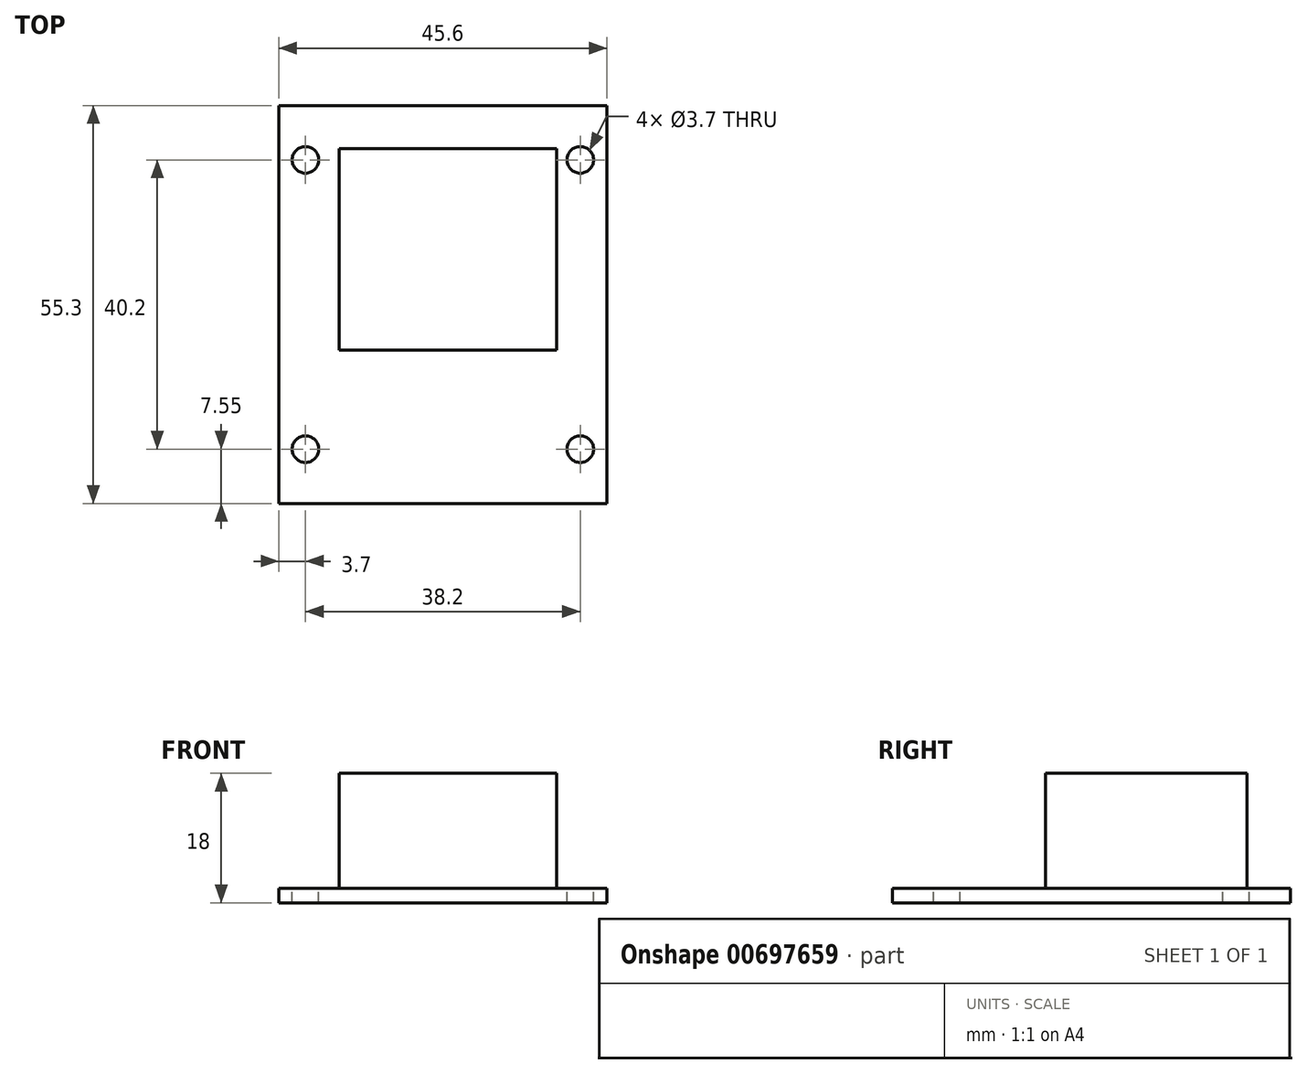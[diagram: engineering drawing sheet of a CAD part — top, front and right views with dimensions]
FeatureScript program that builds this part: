
annotation { "Feature Type Name" : "Feature", "Feature Type Description" : "" }
export const myFeature = defineFeature(function(context is Context, id is Id, definition is map)
    precondition{}
    {
        {
            var Q0;
            Q0=qCreatedBy(makeId("Top.planeOp"),FACE);
            var sketch = newSketch(context, id + "F0", { "sketchPlane" : qUnion([Q0])});
            skLineSegment(sketch, "E0.bottom", {"start": v(22.8, -27.65) * mm, "end": v(-22.8, -27.65) * mm});
            skLineSegment(sketch, "E0.top", {"start": v(22.8, 27.65) * mm, "end": v(-22.8, 27.65) * mm});
            skLineSegment(sketch, "E0.left", {"start": v(22.8, -27.65) * mm, "end": v(22.8, 27.65) * mm});
            skLineSegment(sketch, "E0.right", {"start": v(-22.8, -27.65) * mm, "end": v(-22.8, 27.65) * mm});
            skPoint(sketch, "E0.middle", {"position": v(0, 0) * mm});
            skSolve(sketch);
        }
        {
            var Q0;
            Q0 = qSketchRegion(id + "F0", true);
            extrude(context, id + "F1", {"entities" : qUnion([Q0]), "depth" : 2 * mm, "offsetDistance" : 25 * mm});
        }
        {
            var Q0;
            Q0=makeQuery(id+"F1.opExtrude","CAP_FACE",FACE,{"disambiguationData":[OSD([sQuery(id+"F0.wireOp",EDGE,"E0.bottom"),sQuery(id+"F0.wireOp",EDGE,"E0.top"),sQuery(id+"F0.wireOp",EDGE,"E0.left"),sQuery(id+"F0.wireOp",EDGE,"E0.right")])],"isStart":false});
            var sketch = newSketch(context, id + "F2", { "sketchPlane" : qUnion([Q0])});
            skCircle(sketch, "E1", {"center": v(-19.1, 20.1) * mm, "radius": 1.85 * mm});
            skCircle(sketch, "E2.MirrorC", {"center": v(19.1, 20.1) * mm, "radius": 1.85 * mm});
            skCircle(sketch, "E3.MirrorC", {"center": v(-19.1, -20.1) * mm, "radius": 1.85 * mm});
            skCircle(sketch, "E4.MirrorC", {"center": v(19.1, -20.1) * mm, "radius": 1.85 * mm});
            skSolve(sketch);
        }
        {
            var Q0;
            Q0 = qSketchRegion(id + "F2", true);
            extrude(context, id + "F3", {"entities" : qUnion([Q0]), "operationType" : NewBodyOperationType.REMOVE, "oppositeDirection" : true, "depth" : 25 * mm, "offsetDistance" : 25 * mm});
        }
        {
            var Q0;
            Q0=makeQuery(id+"F1.opExtrude","CAP_FACE",FACE,{"disambiguationData":[OSD([sQuery(id+"F0.wireOp",EDGE,"E0.bottom"),sQuery(id+"F0.wireOp",EDGE,"E0.top"),sQuery(id+"F0.wireOp",EDGE,"E0.left"),sQuery(id+"F0.wireOp",EDGE,"E0.right")])],"isStart":false});
            var sketch = newSketch(context, id + "F4", { "sketchPlane" : qUnion([Q0])});
            skLineSegment(sketch, "E5.bottom", {"start": v(-14.4, 21.65) * mm, "end": v(15.8, 21.65) * mm});
            skLineSegment(sketch, "E5.top", {"start": v(-14.4, -6.35) * mm, "end": v(15.8, -6.35) * mm});
            skLineSegment(sketch, "E5.left", {"start": v(-14.4, 21.65) * mm, "end": v(-14.4, -6.35) * mm});
            skLineSegment(sketch, "E5.right", {"start": v(15.8, 21.65) * mm, "end": v(15.8, -6.35) * mm});
            skSolve(sketch);
        }
        {
            var Q0;
            Q0 = qSketchRegion(id + "F4", true);
            extrude(context, id + "F5", {"entities" : qUnion([Q0]), "operationType" : NewBodyOperationType.ADD, "depth" : 16 * mm, "offsetDistance" : 25 * mm});
        }
    });
